# Revit family: Centerline_Brackets_Floating_Wall_Mount_Universal
name_source: partatom
category: Generic Models
units: mm (PartAtom-declared; Revit-internal decimal feet)

## family parameters
Always vertical = No
Can host rebar = No
Cut with Voids When Loaded = No
Maintain Annotation Orientation = No
Part Type = Normal
Room Calculation Point = No
Round Connector Dimension = Use Diameter
Shared = No
Work Plane-Based = Yes

## types (16) — shared parameters
Construction Details = https://www.arcat.com
Default Elevation = 48 "
Green Building-LEED = https://www.arcat.com
Manufacturer = Centerline Brackets
Manufacturer Fax = 904-429-9450
Manufacturer Website = https://www.countertopbracket.com

## per-type parameters (varying)
| type | Length |
| FWU-R07 | 7 " |
| FWU-R09 | 9 " |
| FWU-R10 | 10 " |
| FWU-R11 | 11 " |
| FWU-R12 | 12 " |
| FWU-R13 | 13 " |
| FWU-R14 | 14 " |
| FWU-R15 | 15 " |
| FWU-R16 | 16 " |
| FWU-R17 | 17 " |
| FWU-R18 | 18 " |
| FWU-R19 | 19 " |
| FWU-R20 | 20 " |
| FWU-R21 | 21 " |
| FWU-R22 | 22 " |
| FWU-R08 | 8 " |

note: column(s) folded — value = type name in every type: Model

## geometry (parser evidence)
native form markers: Sweep x2
no freeform markers — native parametric forms only
